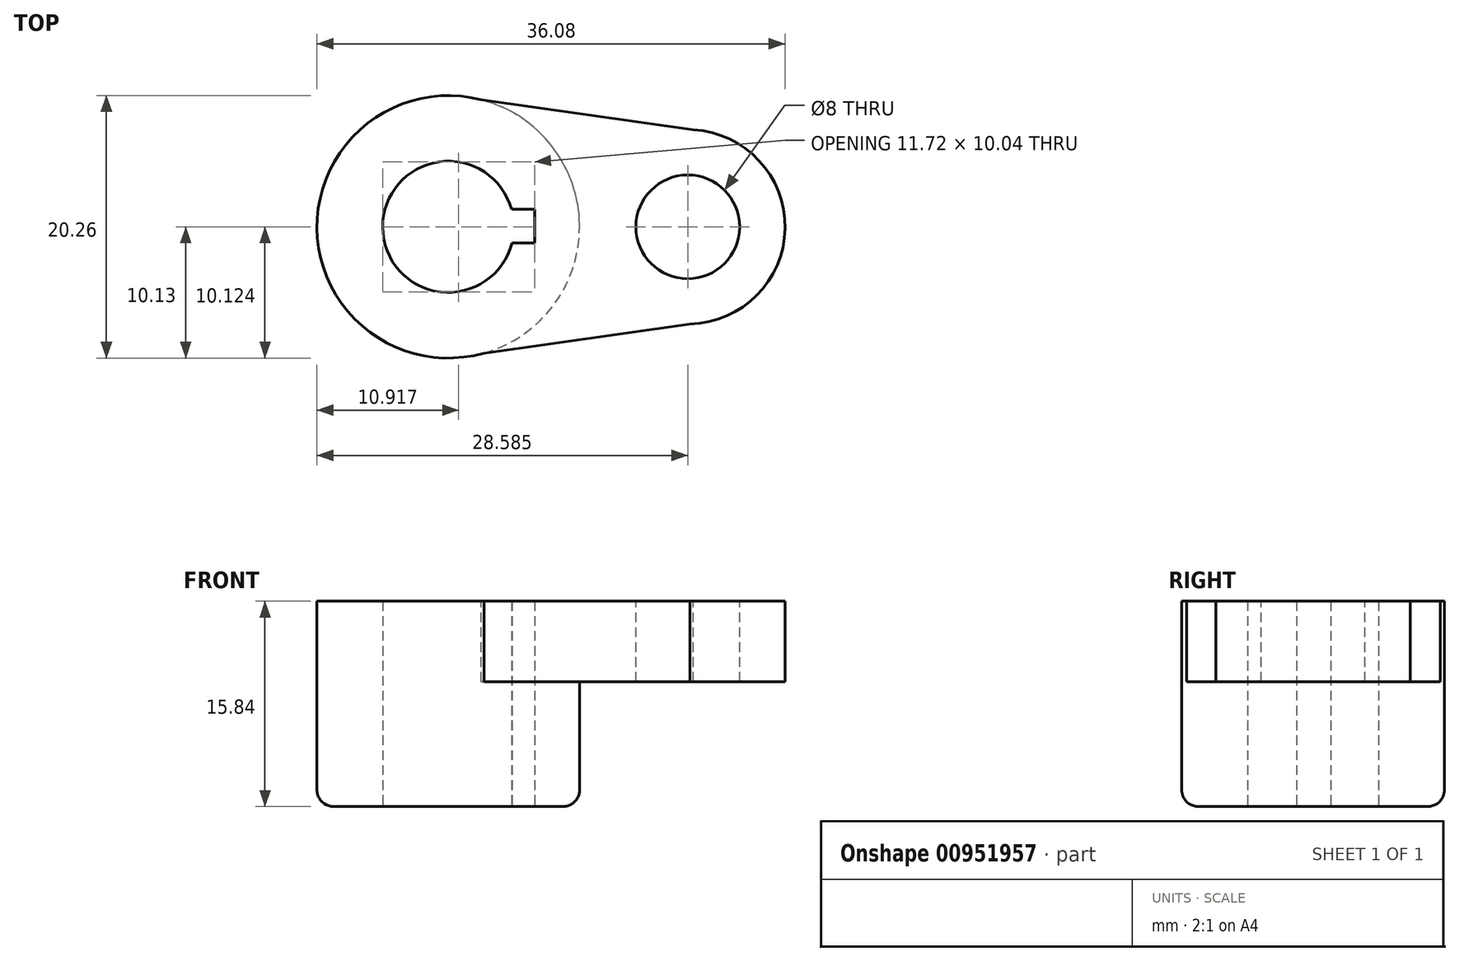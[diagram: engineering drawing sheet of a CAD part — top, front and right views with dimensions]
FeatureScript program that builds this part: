
annotation { "Feature Type Name" : "Feature", "Feature Type Description" : "" }
export const myFeature = defineFeature(function(context is Context, id is Id, definition is map)
    precondition{}
    {
        {
            var Q0;
            Q0=qCreatedBy(makeId("Top.planeOp"),FACE);
            var sketch = newSketch(context, id + "F0", { "sketchPlane" : qUnion([Q0])});
            skCircle(sketch, "E0", {"center": v(-14.4, 0) * mm, "radius": 5.06 * mm});
            skCircle(sketch, "E1", {"center": v(-14.4, 0) * mm, "radius": 10.12 * mm});
            skLineSegment(sketch, "E2", {"start": v(-9.53, 1.35) * mm, "end": v(-7.76, 1.35) * mm});
            skLineSegment(sketch, "E3", {"start": v(-7.76, 1.35) * mm, "end": v(-7.76, -1.26) * mm});
            skLineSegment(sketch, "E4", {"start": v(-7.76, -1.26) * mm, "end": v(-9.5, -1.26) * mm});
            skSolve(sketch);
        }
        {
            var Q0;
            Q0=makeQuery(id+"F0.imprint","IMPRINT",FACE,{"disambiguationData":[TD([[makeQuery(id+"F0.imprint","IMPRINT",EDGE,{"derivedFrom":sQuery(id+"F0.wireOp",EDGE,"E1")}),1.0]])]});
            extrude(context, id + "F1", {"entities" : qUnion([Q0]), "depth" : 15.84 * mm, "offsetDistance" : 25 * mm});
        }
        {
            var Q0;
            Q0=makeQuery(id+"F1.opExtrude","CAP_FACE",FACE,{"disambiguationData":[OSD([sQuery(id+"F0.wireOp",EDGE,"E0"),sQuery(id+"F0.wireOp",EDGE,"E1"),sQuery(id+"F0.wireOp",EDGE,"E2"),sQuery(id+"F0.wireOp",EDGE,"E3"),sQuery(id+"F0.wireOp",EDGE,"E4")])],"isStart":false});
            var sketch = newSketch(context, id + "F2", { "sketchPlane" : qUnion([Q0])});
            skCircle(sketch, "E5", {"center": v(4.05, 0) * mm, "radius": 4 * mm});
            skCircle(sketch, "E6", {"center": v(4.05, 0) * mm, "radius": 7.5 * mm});
            skLineSegment(sketch, "E7", {"start": v(-14.1, 10.12) * mm, "end": v(4.46, 7.49) * mm});
            skLineSegment(sketch, "E8", {"start": v(4.23, -7.5) * mm, "end": v(-14.34, -10.12) * mm});
            skSolve(sketch);
        }
        {
            var Q0;
            Q0=makeQuery(id+"F2.imprint","IMPRINT",FACE,{"disambiguationData":[TD([[makeQuery(id+"F2.imprint","IMPRINT",EDGE,{"derivedFrom":sQuery(id+"F2.wireOp",EDGE,"E5")}),-1.0]])]});
            var Q1;
            {var subQ0=sQuery(id+"F2.wireOp",EDGE,"E7");var subQ1=sQuery(id+"F2.wireOp",EDGE,"E6");var subQ2=makeQuery(id+"F2.imprint","INTERSECT",VERTEX,{"derivedFrom":[subQ1,subQ0]});Q1=makeQuery(id+"F2.imprint","IMPRINT",FACE,{"disambiguationData":[TD([[makeQuery(id+"F2.imprint","IMPRINT",EDGE,{"disambiguationData":[TD([[subQ2,-1.0]])],"derivedFrom":subQ1}),-1.0]])]});}
            extrude(context, id + "F3", {"entities" : qUnion([Q0, Q1]), "operationType" : NewBodyOperationType.ADD, "oppositeDirection" : true, "depth" : 6.2 * mm, "offsetDistance" : 25 * mm});
        }
        {
            var Q0;
            Q0=makeQuery(id+"F1.opExtrude","CAP_EDGE",EDGE,{"disambiguationData":[OSD([sQuery(id+"F0.wireOp",EDGE,"E1")])],"isStart":true});
            fillet(context, id + "F4", {"entities" : qUnion([Q0]), "radius" : 1.3 * mm, "tangentPropagation" : true, "allowEdgeOverflow" : false});
        }
    });
